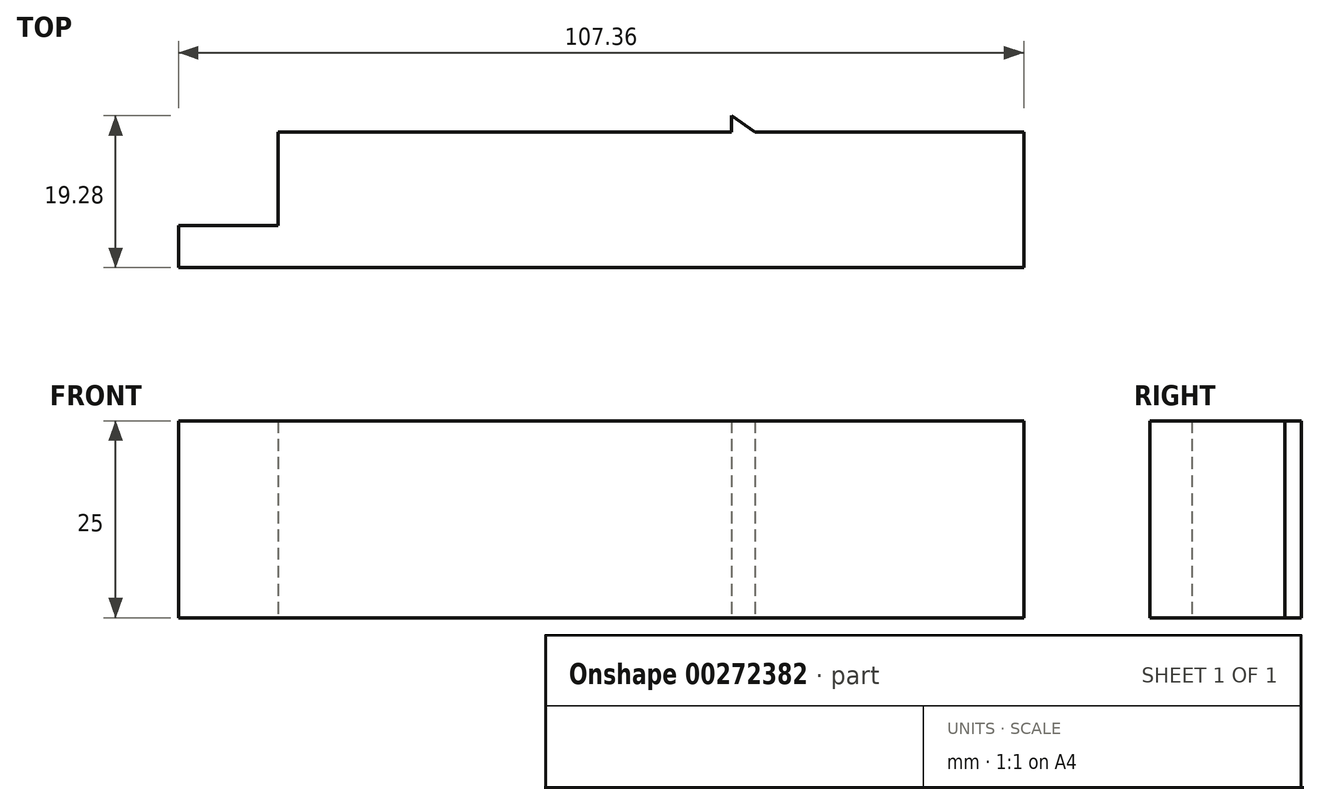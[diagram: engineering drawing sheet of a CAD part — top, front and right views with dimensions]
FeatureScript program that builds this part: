
annotation { "Feature Type Name" : "Feature", "Feature Type Description" : "" }
export const myFeature = defineFeature(function(context is Context, id is Id, definition is map)
    precondition{}
    {
        {
            var Q0;
            Q0=qCreatedBy(makeId("Top.planeOp"),FACE);
            var sketch = newSketch(context, id + "F0", { "sketchPlane" : qUnion([Q0])});
            skLineSegment(sketch, "E0.bottom", {"start": v(53.68, 17.18) * mm, "end": v(-53.68, 17.18) * mm});
            skLineSegment(sketch, "E0.top", {"start": v(53.68, -17.18) * mm, "end": v(-53.68, -17.18) * mm});
            skLineSegment(sketch, "E0.left", {"start": v(53.68, 17.18) * mm, "end": v(53.68, -17.18) * mm});
            skPoint(sketch, "E0.middle", {"position": v(0, 0) * mm});
            skLineSegment(sketch, "E1", {"start": v(-44.15, 0) * mm, "end": v(53.68, 0) * mm});
            skLineSegment(sketch, "E2", {"start": v(-24.87, 0) * mm, "end": v(-44.15, 0) * mm});
            skLineSegment(sketch, "E3", {"start": v(-19.28, 0) * mm, "end": v(53.68, 0) * mm, "construction": true});
            skLineSegment(sketch, "E4", {"start": v(-53.68, -17.18) * mm, "end": v(-53.68, -11.84) * mm});
            skLineSegment(sketch, "E5", {"start": v(-53.68, -11.84) * mm, "end": v(-41.03, -11.84) * mm});
            skLineSegment(sketch, "E6", {"start": v(-41.03, -11.84) * mm, "end": v(-41.03, 0) * mm});
            skLineSegment(sketch, "E7", {"start": v(-41.03, 0) * mm, "end": v(-44.15, 0) * mm});
            skLineSegment(sketch, "E8.MirrorCS", {"start": v(-53.68, -11.84) * mm, "end": v(-66.32, -11.84) * mm});
            skLineSegment(sketch, "E9", {"start": v(-44.15, 1.78) * mm, "end": v(-44.15, 6.96) * mm});
            skLineSegment(sketch, "E10", {"start": v(-44.15, 6.96) * mm, "end": v(-34.71, 6.96) * mm});
            skLineSegment(sketch, "E11", {"start": v(-34.71, 6.96) * mm, "end": v(-34.71, 13.29) * mm});
            skLineSegment(sketch, "E12", {"start": v(-34.71, 13.29) * mm, "end": v(-44.15, 13.29) * mm});
            skLineSegment(sketch, "E13", {"start": v(-44.15, 13.29) * mm, "end": v(-44.15, 19.77) * mm});
            skLineSegment(sketch, "E14", {"start": v(44.23, -17.18) * mm, "end": v(44.23, -4.06) * mm});
            skLineSegment(sketch, "E15", {"start": v(44.23, -4.06) * mm, "end": v(53.68, -4.06) * mm});
            skLineSegment(sketch, "E16", {"start": v(53.68, -4.06) * mm, "end": v(46.34, 3.07) * mm});
            skLineSegment(sketch, "E17", {"start": v(46.34, 3.07) * mm, "end": v(31.1, 4.37) * mm});
            skLineSegment(sketch, "E18", {"start": v(31.1, 4.37) * mm, "end": v(49.42, 9.23) * mm});
            skLineSegment(sketch, "E19", {"start": v(49.42, 9.23) * mm, "end": v(28.35, 13.29) * mm});
            skLineSegment(sketch, "E20", {"start": v(28.02, 12.48) * mm, "end": v(22.84, 5.02) * mm});
            skLineSegment(sketch, "E21", {"start": v(22.84, 5.02) * mm, "end": v(24.3, 2.1) * mm});
            skLineSegment(sketch, "E22", {"start": v(24.3, 2.1) * mm, "end": v(5.81, 13.29) * mm});
            skLineSegment(sketch, "E23", {"start": v(5.81, 13.29) * mm, "end": v(11, 0) * mm});
            skLineSegment(sketch, "E24", {"start": v(11, 0) * mm, "end": v(11, -1.14) * mm});
            skLineSegment(sketch, "E25", {"start": v(16.51, -4.38) * mm, "end": v(16.51, 2.1) * mm});
            skLineSegment(sketch, "E26", {"start": v(16.51, 2.1) * mm, "end": v(44.23, -17.18) * mm});
            skSolve(sketch);
        }
        {
            var Q0;
            Q0 = qSketchRegion(id + "F0", true);
            extrude(context, id + "F1", {"entities" : qUnion([Q0]), "depth" : 25 * mm});
        }
    });
